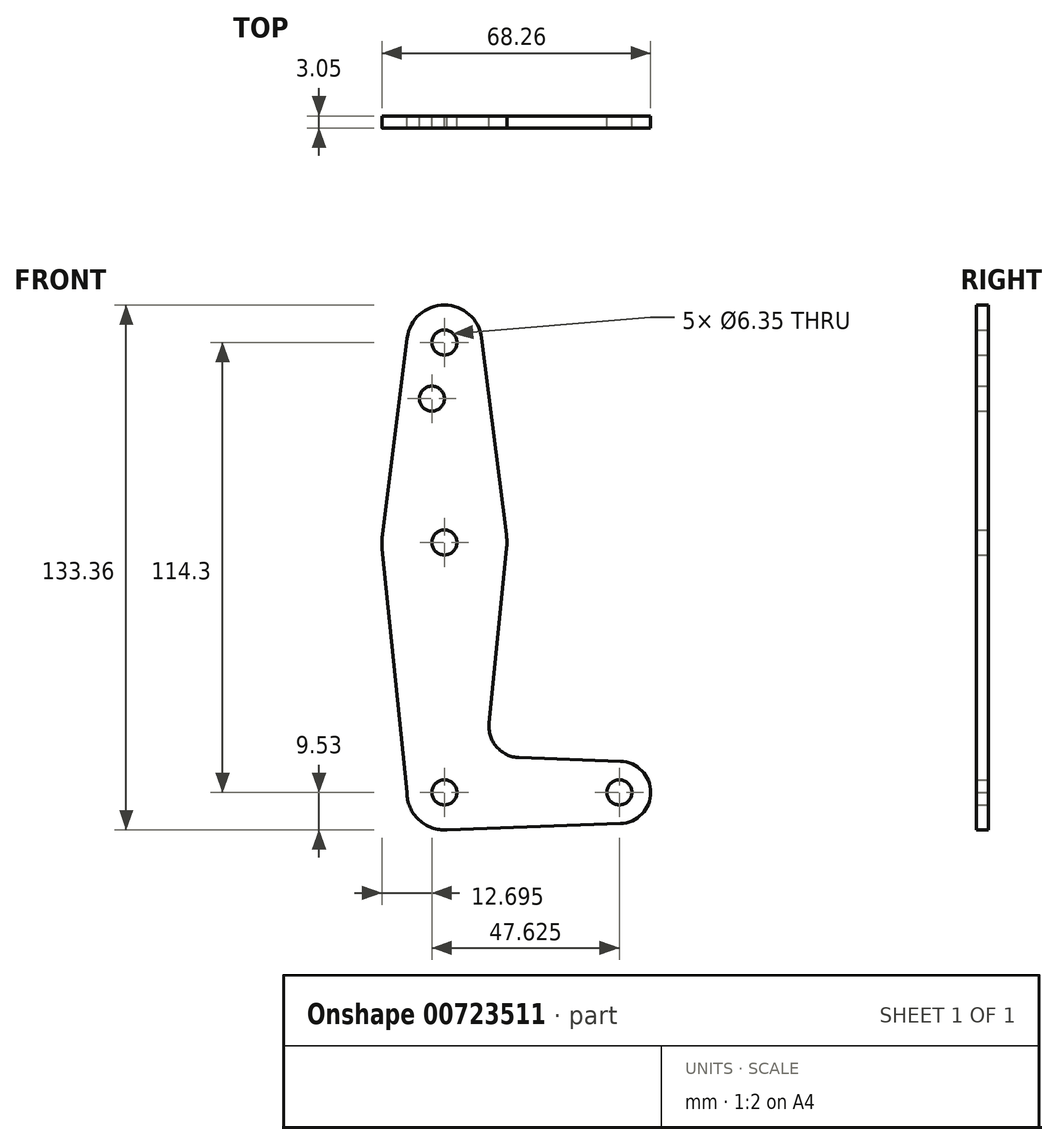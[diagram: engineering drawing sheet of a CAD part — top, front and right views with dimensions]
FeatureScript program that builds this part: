
annotation { "Feature Type Name" : "Feature", "Feature Type Description" : "" }
export const myFeature = defineFeature(function(context is Context, id is Id, definition is map)
    precondition{}
    {
        {
            var Q0;
            Q0=qCreatedBy(makeId("Front.planeOp"),FACE);
            var sketch = newSketch(context, id + "F0", { "sketchPlane" : qUnion([Q0])});
            skLineSegment(sketch, "E0", {"start": v(0, 114.3) * mm, "end": v(0, 0) * mm, "construction": true});
            skLineSegment(sketch, "E1", {"start": v(0, 0) * mm, "end": v(44.45, 0) * mm, "construction": true});
            skCircle(sketch, "E2", {"center": v(0, 114.3) * mm, "radius": 9.53 * mm});
            skCircle(sketch, "E3", {"center": v(0, 0) * mm, "radius": 9.53 * mm});
            skCircle(sketch, "E4", {"center": v(44.45, 0) * mm, "radius": 7.94 * mm});
            skCircle(sketch, "E5", {"center": v(0, 63.5) * mm, "radius": 15.88 * mm});
            skLineSegment(sketch, "E6", {"start": v(-9.53, 0) * mm, "end": v(-15.8, 61.9) * mm});
            skLineSegment(sketch, "E7", {"start": v(18.97, 8.85) * mm, "end": v(44.73, 7.93) * mm});
            skLineSegment(sketch, "E8", {"start": v(0, -9.53) * mm, "end": v(44.73, -7.93) * mm});
            skLineSegment(sketch, "E9", {"start": v(9.45, 115.5) * mm, "end": v(15.75, 65.48) * mm});
            skLineSegment(sketch, "E10", {"start": v(15.8, 61.91) * mm, "end": v(11.34, 17.59) * mm});
            skLineSegment(sketch, "E11", {"start": v(-9.45, 115.5) * mm, "end": v(-15.75, 65.48) * mm});
            skCircle(sketch, "E12", {"center": v(0, 114.3) * mm, "radius": 3.18 * mm});
            skCircle(sketch, "E13", {"center": v(-3.17, 100.03) * mm, "radius": 3.18 * mm});
            skCircle(sketch, "E14", {"center": v(0, 63.5) * mm, "radius": 3.18 * mm});
            skCircle(sketch, "E15", {"center": v(0, 0) * mm, "radius": 3.18 * mm});
            skCircle(sketch, "E16", {"center": v(44.45, 0) * mm, "radius": 3.18 * mm});
            skArc(sketch, "E17.filletArc", {"start": v(11.34, 17.59) * mm, "mid": v(13.26, 11.57) * mm, "end": v(18.97, 8.85) * mm});
            skSolve(sketch);
        }
        {
            var Q0;
            Q0 = qSketchRegion(id + "F0", true);
            extrude(context, id + "F1", {"entities" : qUnion([Q0]), "depth" : 3.05 * mm, "offsetDistance" : 25.4 * mm});
        }
    });
